# Revit family: Studio-Patio-Door_XOO-2.625-Sill
name_source: partatom
category: Doors
units: mm (PartAtom-declared; Revit-internal decimal feet)

## family parameters
Always vertical = Yes
Classification Number = 23.30.10.00
Cut with Voids When Loaded = No
Host = Wall
Room Calculation Point = No
Shared = No

## types (12) — shared parameters
Analytic Construction = <None>
Define Thermal Properties by = Schematic Type
Door Height = 76 "
Function = Interior
Glass Material = Glass
Height = 80 "
Height Sash = 76 "
Manufacturer = Novatech Group
Model = ƒif(([6p vs 7.25p]), "Urbania/Loft 6p", "Urbania/Loft 71/4p")
URL = https://www.groupenovatech.com
Wall Closure = By host

## per-type parameters (varying)
| type | Door Width | Frame Material | Width | Width Sash |
| Custom Color - 88 3/4" × 79 1/2" | 30 " | Custom Color | 89 " | 30 " |
| Custom Color - 106 3/4" × 79 1/2" | 36 " | Custom Color | 107 " | 36 " |
| Custom Color - 142 3/4" × 79 1/2" | 48 " | Custom Color | 143 " | 48 " |
| Clear anodized - 142 3/4" × 79 1/2" | 48 " | Clear anodized | 143 " | 48 " |
| Clear anodized - 106 3/4" × 79 1/2" | 36 " | Clear anodized | 107 " | 36 " |
| Clear anodized - 88 3/4" × 79 1/2" | 30 " | Clear anodized | 89 " | 30 " |
| Black - 88 3/4" × 79 1/2" | 30 " | Black | 89 " | 30 " |
| Black - 106 3/4" × 79 1/2" | 36 " | Black | 107 " | 36 " |
| Black - 142 3/4" × 79 1/2" | 48 " | Black | 143 " | 48 " |
| Commercial Brown - 142 3/4" × 79 1/2" | 48 " | Commercial Brown | 143 " | 48 " |
| Commercial Brown - 106 3/4" × 79 1/2" | 36 " | Commercial Brown | 107 " | 36 " |
| Commercial Brown - 88 3/4" × 79 1/2" | 30 " | Commercial Brown | 89 " | 30 " |

## geometry (parser evidence)
native form markers: Sweep x5
no freeform markers — native parametric forms only
